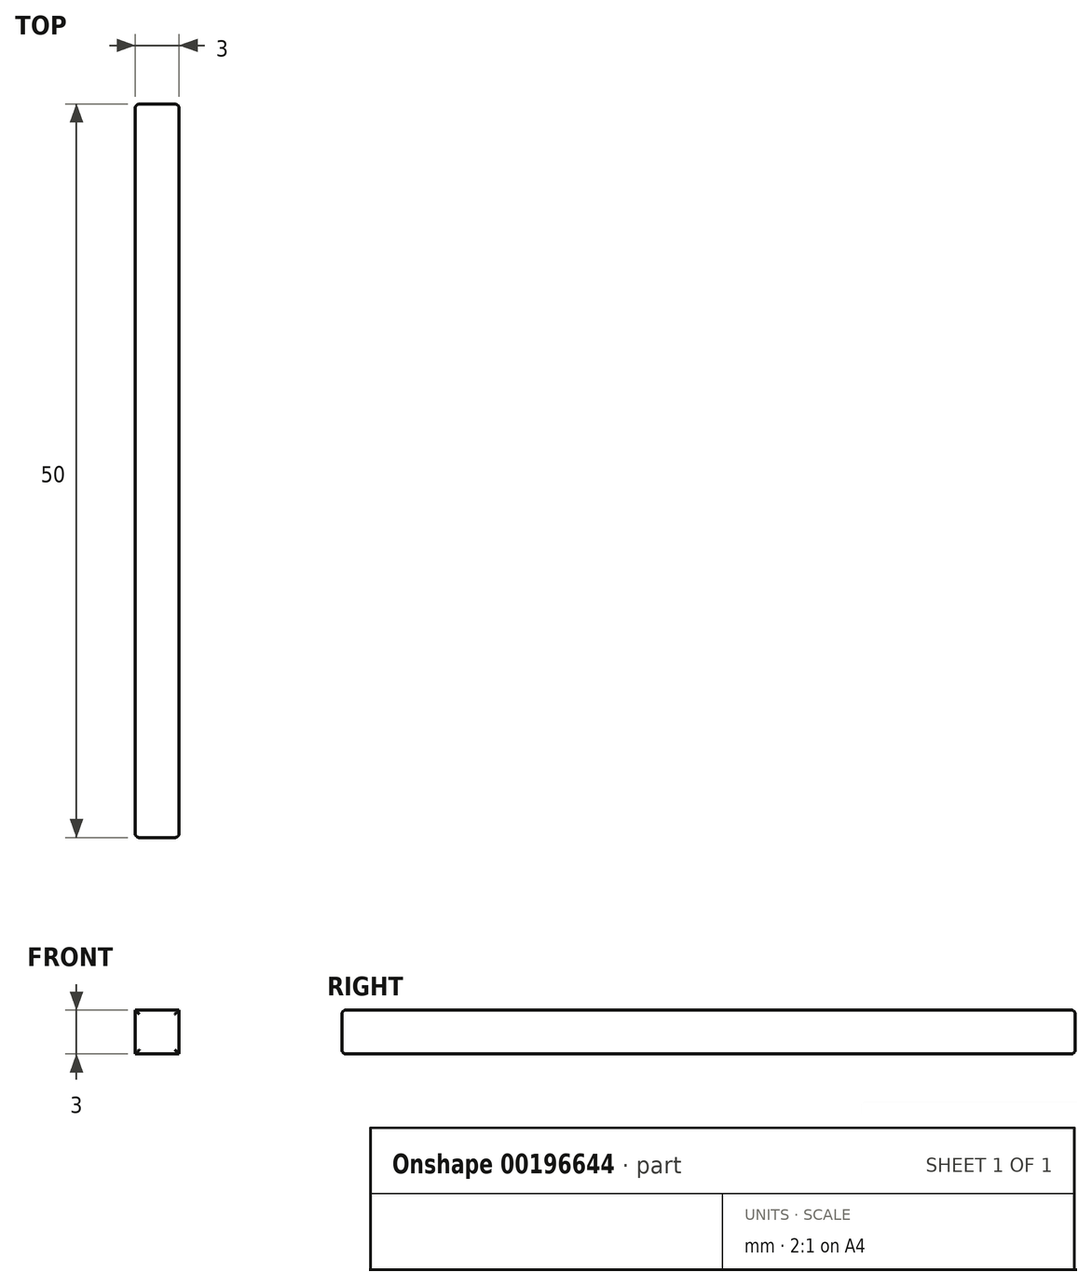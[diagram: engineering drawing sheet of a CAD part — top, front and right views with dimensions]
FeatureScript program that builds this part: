
annotation { "Feature Type Name" : "Feature", "Feature Type Description" : "" }
export const myFeature = defineFeature(function(context is Context, id is Id, definition is map)
    precondition{}
    {
        {
            var Q0;
            Q0=qCreatedBy(makeId("Front.planeOp"),FACE);
            var sketch = newSketch(context, id + "F0", { "sketchPlane" : qUnion([Q0])});
            skLineSegment(sketch, "E0.bottom", {"start": v(-1.5, 3) * mm, "end": v(1.5, 3) * mm});
            skLineSegment(sketch, "E0.top", {"start": v(-1.5, 0) * mm, "end": v(1.5, 0) * mm});
            skLineSegment(sketch, "E0.left", {"start": v(-1.5, 3) * mm, "end": v(-1.5, 0) * mm});
            skLineSegment(sketch, "E0.right", {"start": v(1.5, 3) * mm, "end": v(1.5, 0) * mm});
            skSolve(sketch);
        }
        {
            var Q0;
            Q0 = qSketchRegion(id + "F0", true);
            extrude(context, id + "F1", {"entities" : qUnion([Q0]), "depth" : 50 * mm});
        }
        {
            var Q0;
            Q0=makeQuery(id+"F1.opExtrude","CAP_EDGE",EDGE,{"disambiguationData":[OSD([sQuery(id+"F0.wireOp",EDGE,"E0.bottom")])],"isStart":true});
            var Q1;
            Q1=makeQuery(id+"F1.opExtrude","CAP_EDGE",EDGE,{"disambiguationData":[OSD([sQuery(id+"F0.wireOp",EDGE,"E0.left")])],"isStart":true});
            var Q2;
            Q2=makeQuery(id+"F1.opExtrude","CAP_EDGE",EDGE,{"disambiguationData":[OSD([sQuery(id+"F0.wireOp",EDGE,"E0.right")])],"isStart":true});
            var Q3;
            Q3=makeQuery(id+"F1.opExtrude","CAP_EDGE",EDGE,{"disambiguationData":[OSD([sQuery(id+"F0.wireOp",EDGE,"E0.top")])],"isStart":true});
            var Q4;
            Q4=makeQuery(id+"F1.opExtrude","CAP_EDGE",EDGE,{"disambiguationData":[OSD([sQuery(id+"F0.wireOp",EDGE,"E0.bottom")])],"isStart":false});
            var Q5;
            Q5=makeQuery(id+"F1.opExtrude","CAP_EDGE",EDGE,{"disambiguationData":[OSD([sQuery(id+"F0.wireOp",EDGE,"E0.right")])],"isStart":false});
            var Q6;
            Q6=makeQuery(id+"F1.opExtrude","CAP_EDGE",EDGE,{"disambiguationData":[OSD([sQuery(id+"F0.wireOp",EDGE,"E0.left")])],"isStart":false});
            var Q7;
            Q7=makeQuery(id+"F1.opExtrude","CAP_FACE",FACE,{"disambiguationData":[OSD([sQuery(id+"F0.wireOp",EDGE,"E0.bottom"),sQuery(id+"F0.wireOp",EDGE,"E0.top"),sQuery(id+"F0.wireOp",EDGE,"E0.left"),sQuery(id+"F0.wireOp",EDGE,"E0.right")])],"isStart":false});
            fillet(context, id + "F2", {"entities" : qUnion([Q0, Q1, Q2, Q3, Q4, Q5, Q6, Q7]), "radius" : 0.3 * mm, "tangentPropagation" : true, "allowEdgeOverflow" : false});
        }
    });
